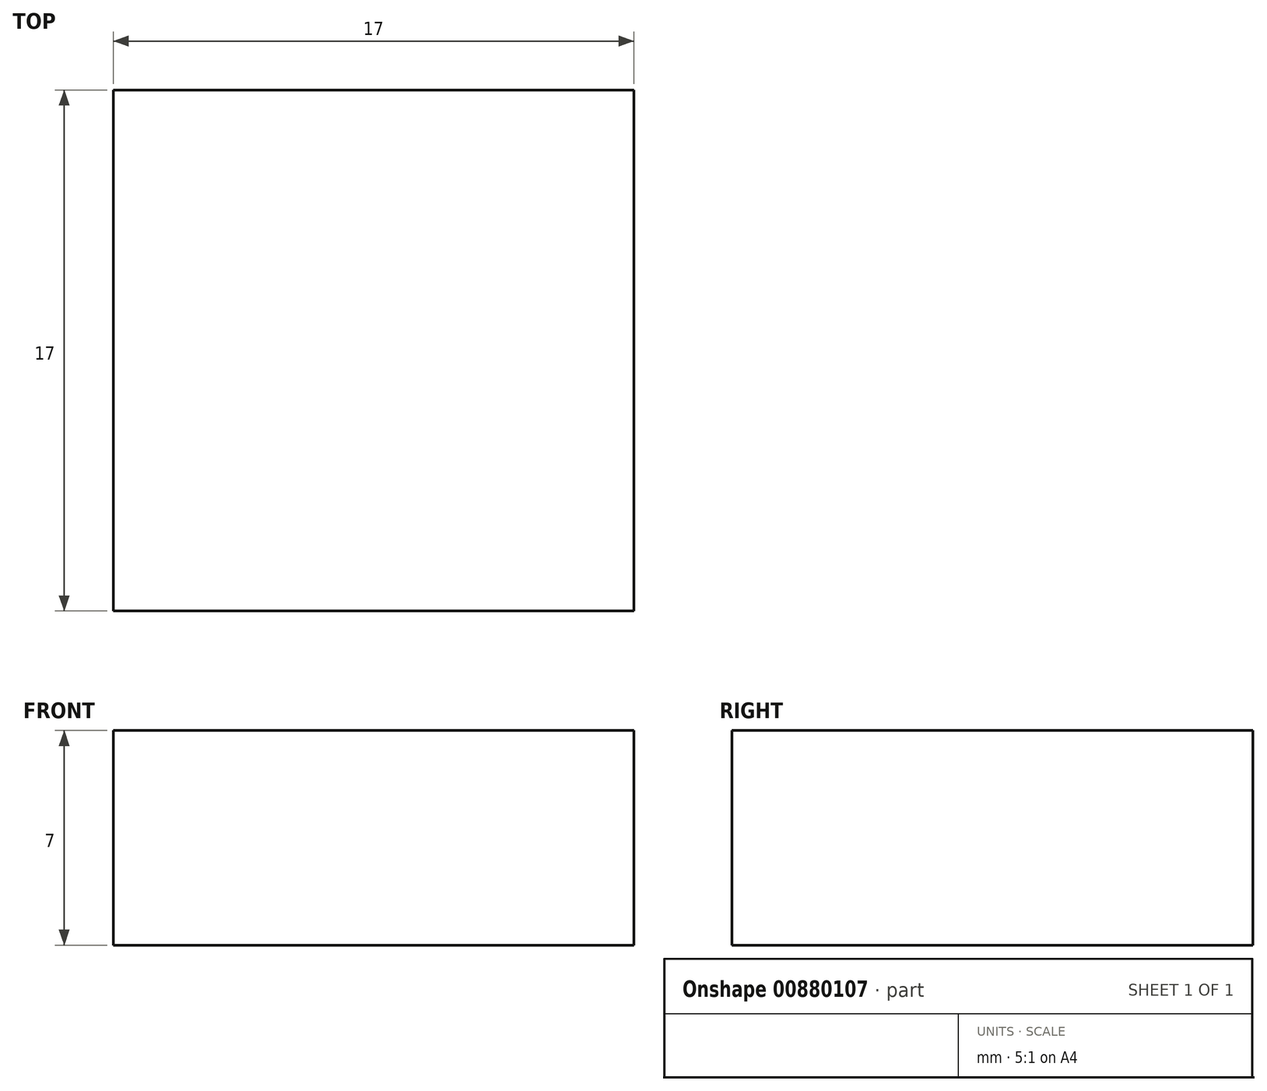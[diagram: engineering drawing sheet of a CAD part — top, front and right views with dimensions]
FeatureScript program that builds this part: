
annotation { "Feature Type Name" : "Feature", "Feature Type Description" : "" }
export const myFeature = defineFeature(function(context is Context, id is Id, definition is map)
    precondition{}
    {
        {
            var Q0;
            Q0=qCreatedBy(makeId("Top.planeOp"),FACE);
            var sketch = newSketch(context, id + "F0", { "sketchPlane" : qUnion([Q0])});
            skLineSegment(sketch, "E0.bottom", {"start": v(8.5, -8.5) * mm, "end": v(-8.5, -8.5) * mm});
            skLineSegment(sketch, "E0.top", {"start": v(8.5, 8.5) * mm, "end": v(-8.5, 8.5) * mm});
            skLineSegment(sketch, "E0.left", {"start": v(8.5, -8.5) * mm, "end": v(8.5, 8.5) * mm});
            skLineSegment(sketch, "E0.right", {"start": v(-8.5, -8.5) * mm, "end": v(-8.5, 8.5) * mm});
            skPoint(sketch, "E0.middle", {"position": v(0, 0) * mm});
            skSolve(sketch);
        }
        {
            var Q0;
            Q0=makeQuery(id+"F0.imprint","IMPRINT",FACE,{"disambiguationData":[TD([[makeQuery(id+"F0.imprint","IMPRINT",EDGE,{"derivedFrom":sQuery(id+"F0.wireOp",EDGE,"E0.bottom")}),-1.0]])]});
            extrude(context, id + "F1", {"entities" : qUnion([Q0]), "depth" : 7 * mm, "offsetDistance" : 25 * mm});
        }
    });
